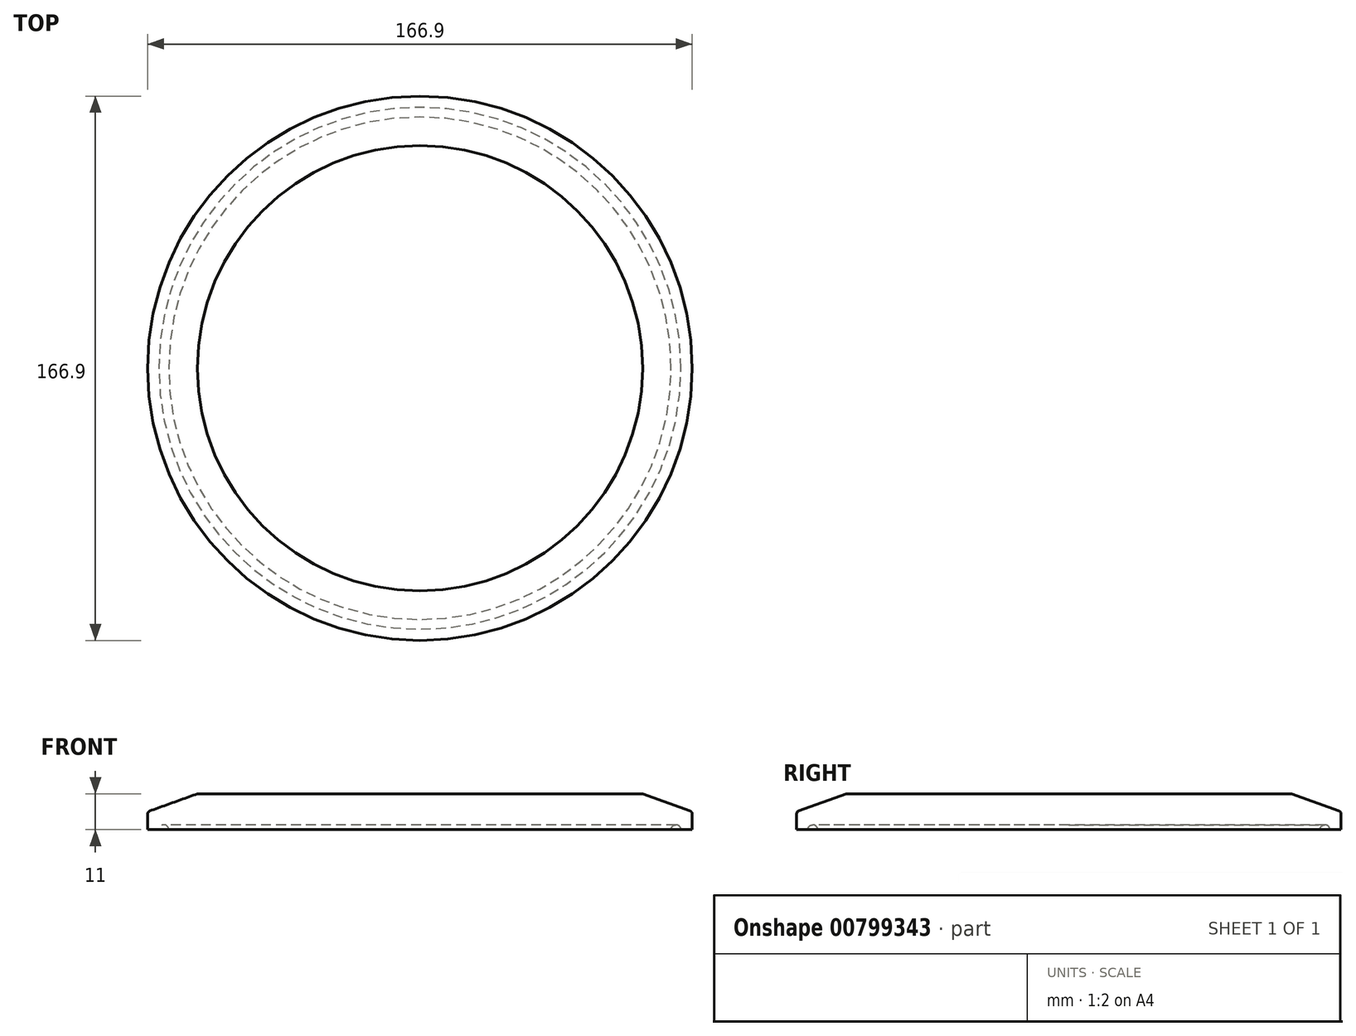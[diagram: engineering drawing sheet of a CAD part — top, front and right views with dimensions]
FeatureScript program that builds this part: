
annotation { "Feature Type Name" : "Feature", "Feature Type Description" : "" }
export const myFeature = defineFeature(function(context is Context, id is Id, definition is map)
    precondition{}
    {
        {
            var Q0;
            Q0=qCreatedBy(makeId("Front.planeOp"),FACE);
            var sketch = newSketch(context, id + "F0", { "sketchPlane" : qUnion([Q0])});
            skLineSegment(sketch, "E0", {"start": v(-83.45, 0) * mm, "end": v(-83.45, 4.8) * mm});
            skPoint(sketch, "E0.endSnap0", {"position": v(-68.25, 5.5) * mm});
            skLineSegment(sketch, "E1", {"start": v(-68.25, 11) * mm, "end": v(-82.8, 5.74) * mm});
            skArc(sketch, "E2", {"start": v(-77, 0) * mm, "mid": v(-78.5, 1.5) * mm, "end": v(-80, 0) * mm});
            skLineSegment(sketch, "E3.trimOffspring", {"start": v(-80, 0) * mm, "end": v(-83.45, 0) * mm});
            skLineSegment(sketch, "E4", {"start": v(0, 0) * mm, "end": v(0, 38.79) * mm, "construction": true});
            skLineSegment(sketch, "E5", {"start": v(-68.25, 11) * mm, "end": v(0, 11) * mm});
            skLineSegment(sketch, "E6", {"start": v(-77, 0) * mm, "end": v(0, 0) * mm});
            skLineSegment(sketch, "E7", {"start": v(0, 11) * mm, "end": v(0, 0) * mm});
            skLineSegment(sketch, "E8", {"start": v(-80, 0) * mm, "end": v(-77, 0) * mm, "construction": true});
            skPoint(sketch, "E9.visualSharp", {"position": v(-83.45, 5.5) * mm});
            skArc(sketch, "E9.filletArc", {"start": v(-82.8, 5.74) * mm, "mid": v(-83.27, 5.37) * mm, "end": v(-83.45, 4.8) * mm});
            skSolve(sketch);
        }
        {
            var Q0;
            Q0=qSketchRegion(id+"F0",true);
            var Q1;
            Q1=sQuery(id+"F0.wireOp",EDGE,"E4");
            revolve(context, id + "F1", {"entities" : qUnion([Q0]), "axis" : qUnion([Q1]), "revolveType" : RevolveType.FULL});
        }
    });
